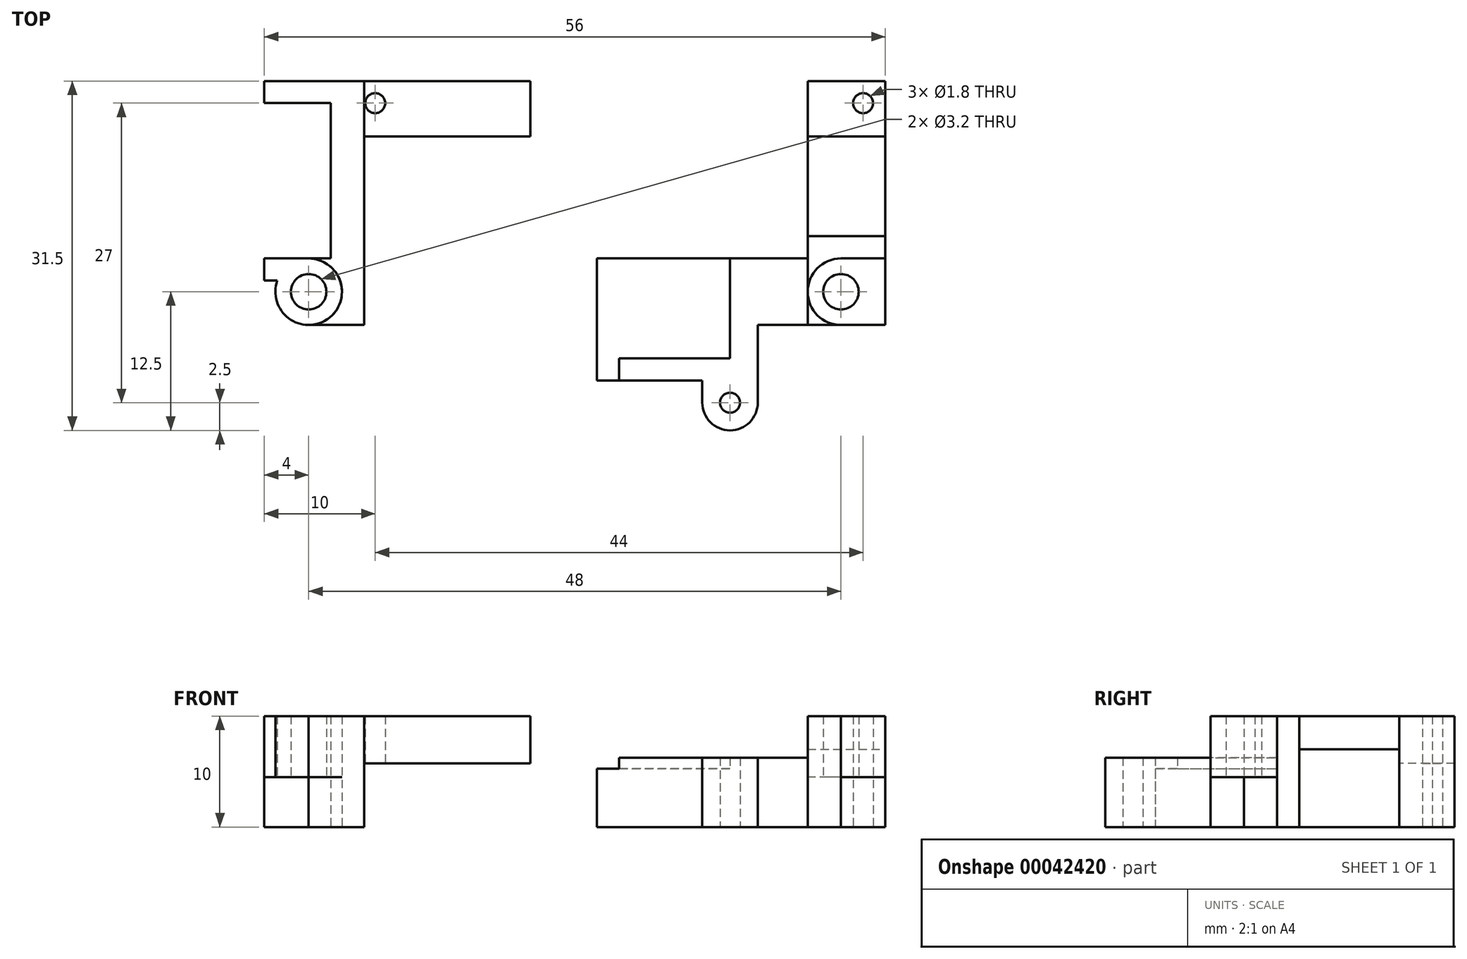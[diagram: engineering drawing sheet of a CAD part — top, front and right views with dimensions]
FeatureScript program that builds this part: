
annotation { "Feature Type Name" : "Feature", "Feature Type Description" : "" }
export const myFeature = defineFeature(function(context is Context, id is Id, definition is map)
    precondition{}
    {
        {
            var Q0;
            Q0=qCreatedBy(makeId("Top.planeOp"),FACE);
            var sketch = newSketch(context, id + "F0", { "sketchPlane" : qUnion([Q0])});
            skCircle(sketch, "E0", {"center": v(-24, 0) * mm, "radius": 1.6 * mm});
            skCircle(sketch, "E1", {"center": v(24, 0) * mm, "radius": 1.6 * mm});
            skCircle(sketch, "E2", {"center": v(26, 17) * mm, "radius": 0.9 * mm});
            skCircle(sketch, "E3", {"center": v(-24, 0) * mm, "radius": 3 * mm});
            skCircle(sketch, "E4", {"center": v(24, 0) * mm, "radius": 3 * mm});
            skLineSegment(sketch, "E5", {"start": v(-19, 19) * mm, "end": v(-19, -3) * mm});
            skLineSegment(sketch, "E6", {"start": v(-19, -3) * mm, "end": v(-24, -3) * mm});
            skLineSegment(sketch, "E7", {"start": v(2, 32) * mm, "end": v(2, -35.95) * mm, "construction": true});
            skLineSegment(sketch, "E8", {"start": v(2, -8) * mm, "end": v(-19, -8) * mm, "construction": true});
            skLineSegment(sketch, "E9", {"start": v(-19, -3) * mm, "end": v(-19, -8) * mm, "construction": true});
            skLineSegment(sketch, "E10", {"start": v(28, 3) * mm, "end": v(2, 3) * mm});
            skLineSegment(sketch, "E11", {"start": v(28, -3) * mm, "end": v(14, -3) * mm});
            skLineSegment(sketch, "E12", {"start": v(2, -3) * mm, "end": v(2, 3) * mm});
            skLineSegment(sketch, "E13", {"start": v(26, 17) * mm, "end": v(-28.96, 17) * mm, "construction": true});
            skLineSegment(sketch, "E14", {"start": v(-28, 33.68) * mm, "end": v(-28, -20.87) * mm, "construction": true});
            skLineSegment(sketch, "E15", {"start": v(-19, 3) * mm, "end": v(-28, 3) * mm});
            skLineSegment(sketch, "E16", {"start": v(-28, 3) * mm, "end": v(-28, 1) * mm});
            skLineSegment(sketch, "E17", {"start": v(-19, 19) * mm, "end": v(-22, 19) * mm});
            skLineSegment(sketch, "E18", {"start": v(-22, 19) * mm, "end": v(-22, 3) * mm});
            skLineSegment(sketch, "E19", {"start": v(-22, 19) * mm, "end": v(-28, 19) * mm});
            skLineSegment(sketch, "E20", {"start": v(-28, 19) * mm, "end": v(-28, 17) * mm});
            skLineSegment(sketch, "E21", {"start": v(-28, 17) * mm, "end": v(-22, 17) * mm});
            skLineSegment(sketch, "E22", {"start": v(21, 0) * mm, "end": v(21, -3) * mm});
            skCircle(sketch, "E23", {"center": v(14, -10) * mm, "radius": 0.9 * mm});
            skCircle(sketch, "E24", {"center": v(14, -10) * mm, "radius": 2.5 * mm});
            skLineSegment(sketch, "E25", {"start": v(16.5, -3) * mm, "end": v(16.5, -10) * mm});
            skLineSegment(sketch, "E26", {"start": v(2, -3) * mm, "end": v(2, -8) * mm});
            skLineSegment(sketch, "E27", {"start": v(-21, 3) * mm, "end": v(-21, 0) * mm});
            skLineSegment(sketch, "E28", {"start": v(-21, -3) * mm, "end": v(-21, 0) * mm});
            skLineSegment(sketch, "E29", {"start": v(-19, 19) * mm, "end": v(-4, 19) * mm});
            skLineSegment(sketch, "E30", {"start": v(-4, 19) * mm, "end": v(-4, 14) * mm});
            skLineSegment(sketch, "E31", {"start": v(-4, 14) * mm, "end": v(-19, 14) * mm});
            skLineSegment(sketch, "E32", {"start": v(28, -3) * mm, "end": v(28, 3) * mm});
            skLineSegment(sketch, "E33", {"start": v(28, 3) * mm, "end": v(28, 19) * mm});
            skLineSegment(sketch, "E34", {"start": v(28, 19) * mm, "end": v(21, 19) * mm});
            skLineSegment(sketch, "E35", {"start": v(21, 19) * mm, "end": v(21, 0) * mm});
            skCircle(sketch, "E36", {"center": v(26, 17) * mm, "radius": 1.5 * mm});
            skLineSegment(sketch, "E37", {"start": v(21, 14) * mm, "end": v(28, 14) * mm});
            skLineSegment(sketch, "E38", {"start": v(21, 5) * mm, "end": v(28, 5) * mm});
            skCircle(sketch, "E39", {"center": v(-18, 17) * mm, "radius": 0.9 * mm});
            skLineSegment(sketch, "E40", {"start": v(14, -6) * mm, "end": v(14, 3) * mm});
            skLineSegment(sketch, "E41", {"start": v(4, -6) * mm, "end": v(14, -6) * mm});
            skLineSegment(sketch, "E42", {"start": v(11.5, -8) * mm, "end": v(11.5, -10) * mm});
            skLineSegment(sketch, "E43", {"start": v(2, -8) * mm, "end": v(11.5, -8) * mm});
            skLineSegment(sketch, "E44", {"start": v(4, -6) * mm, "end": v(4, -8) * mm});
            skLineSegment(sketch, "E45", {"start": v(-28, 1) * mm, "end": v(-26.83, 1) * mm});
            skSolve(sketch);
        }
        {
            var Q0;
            {var subQ1=sQuery(id+"F0.wireOp",EDGE,"E29");Q0=makeQuery(id+"F0.imprint","IMPRINT",FACE,{"disambiguationData":[TD([[makeQuery(id+"F0.imprint","IMPRINT",EDGE,{"derivedFrom":subQ1}),-1.0]])]});}
            extrude(context, id + "F1", {"entities" : qUnion([Q0]), "depth" : 10 * mm, "hasSecondDirection" : true, "secondDirectionOppositeDirection" : false, "secondDirectionDepth" : 5.75 * mm});
        }
        {
            var Q0;
            {var subQ4=sQuery(id+"F0.wireOp",EDGE,"E25");Q0=makeQuery(id+"F0.imprint","IMPRINT",FACE,{"disambiguationData":[TD([[makeQuery(id+"F0.imprint","IMPRINT",EDGE,{"derivedFrom":subQ4}),-1.0]])]});}
            var Q1;
            Q1=makeQuery(id+"F0.imprint","IMPRINT",FACE,{"disambiguationData":[TD([[makeQuery(id+"F0.imprint","IMPRINT",EDGE,{"derivedFrom":sQuery(id+"F0.wireOp",EDGE,"E23")}),-1.0]])]});
            var Q2;
            {var subQ5=sQuery(id+"F0.wireOp",EDGE,"E22");Q2=makeQuery(id+"F0.imprint","IMPRINT",FACE,{"disambiguationData":[TD([[makeQuery(id+"F0.imprint","IMPRINT",EDGE,{"derivedFrom":subQ5}),-1.0]])]});}
            extrude(context, id + "F2", {"entities" : qUnion([Q0, Q1, Q2]), "depth" : 6.25 * mm});
        }
        {
            var Q0;
            {var subQ1=sQuery(id+"F0.wireOp",EDGE,"E37");Q0=makeQuery(id+"F0.imprint","IMPRINT",FACE,{"disambiguationData":[TD([[makeQuery(id+"F0.imprint","IMPRINT",EDGE,{"derivedFrom":subQ1}),-1.0]])]});}
            extrude(context, id + "F3", {"entities" : qUnion([Q0]), "depth" : 7 * mm});
        }
        {
            var Q0;
            {var subQ8=sQuery(id+"F0.wireOp",EDGE,"E12");Q0=makeQuery(id+"F0.imprint","IMPRINT",FACE,{"disambiguationData":[TD([[makeQuery(id+"F0.imprint","IMPRINT",EDGE,{"derivedFrom":subQ8}),-1.0]])]});}
            extrude(context, id + "F4", {"entities" : qUnion([Q0]), "operationType" : NewBodyOperationType.ADD, "depth" : 5.25 * mm});
        }
        {
            var Q0;
            {var subQ1=sQuery(id+"F0.wireOp",EDGE,"E19");Q0=makeQuery(id+"F0.imprint","IMPRINT",FACE,{"disambiguationData":[TD([[makeQuery(id+"F0.imprint","IMPRINT",EDGE,{"derivedFrom":subQ1}),1.0]])]});}
            var Q1;
            {var subQ0=sQuery(id+"F0.wireOp",EDGE,"E17");Q1=makeQuery(id+"F0.imprint","IMPRINT",FACE,{"disambiguationData":[TD([[makeQuery(id+"F0.imprint","IMPRINT",EDGE,{"derivedFrom":subQ0}),1.0]])]});}
            var Q2;
            {var subQ6=sQuery(id+"F0.wireOp",EDGE,"E27");Q2=makeQuery(id+"F0.imprint","IMPRINT",FACE,{"disambiguationData":[TD([[makeQuery(id+"F0.imprint","IMPRINT",EDGE,{"derivedFrom":subQ6}),1.0]])]});}
            var Q3;
            {var subQ0=sQuery(id+"F0.wireOp",EDGE,"E27");Q3=makeQuery(id+"F0.imprint","IMPRINT",FACE,{"disambiguationData":[TD([[makeQuery(id+"F0.imprint","IMPRINT",EDGE,{"derivedFrom":subQ0}),-1.0]])]});}
            var Q4;
            {var subQ0=sQuery(id+"F0.wireOp",EDGE,"E28");Q4=makeQuery(id+"F0.imprint","IMPRINT",FACE,{"disambiguationData":[TD([[makeQuery(id+"F0.imprint","IMPRINT",EDGE,{"derivedFrom":subQ0}),1.0]])]});}
            var Q5;
            {var subQ2=sQuery(id+"F0.wireOp",EDGE,"E34");Q5=makeQuery(id+"F0.imprint","IMPRINT",FACE,{"disambiguationData":[TD([[makeQuery(id+"F0.imprint","IMPRINT",EDGE,{"derivedFrom":subQ2}),1.0]])]});}
            var Q6;
            Q6=makeQuery(id+"F0.imprint","IMPRINT",FACE,{"disambiguationData":[TD([[makeQuery(id+"F0.imprint","IMPRINT",EDGE,{"derivedFrom":sQuery(id+"F0.wireOp",EDGE,"E2")}),-1.0]])]});
            var Q7;
            {var subQ0=sQuery(id+"F0.wireOp",EDGE,"E38");Q7=makeQuery(id+"F0.imprint","IMPRINT",FACE,{"disambiguationData":[TD([[makeQuery(id+"F0.imprint","IMPRINT",EDGE,{"derivedFrom":subQ0}),-1.0]])]});}
            var Q8;
            {var subQ0=sQuery(id+"F0.wireOp",EDGE,"E35");var subQ1=sQuery(id+"F0.wireOp",EDGE,"E10");var subQ2=makeQuery(id+"F0.imprint","INTERSECT",VERTEX,{"derivedFrom":[subQ1,subQ0]});Q8=makeQuery(id+"F0.imprint","IMPRINT",FACE,{"disambiguationData":[TD([[makeQuery(id+"F0.imprint","IMPRINT",EDGE,{"disambiguationData":[TD([[subQ2,1.0]])],"derivedFrom":subQ1}),1.0]])]});}
            var Q9;
            {var subQ0=sQuery(id+"F0.wireOp",EDGE,"E22");Q9=makeQuery(id+"F0.imprint","IMPRINT",FACE,{"disambiguationData":[TD([[makeQuery(id+"F0.imprint","IMPRINT",EDGE,{"derivedFrom":subQ0}),1.0]])]});}
            extrude(context, id + "F5", {"entities" : qUnion([Q0, Q1, Q2, Q3, Q4, Q5, Q6, Q7, Q8, Q9]), "depth" : 10 * mm});
        }
        {
            var Q0;
            Q0=makeQuery(id+"F0.imprint","IMPRINT",FACE,{"disambiguationData":[TD([[makeQuery(id+"F0.imprint","IMPRINT",EDGE,{"derivedFrom":sQuery(id+"F0.wireOp",EDGE,"E0")}),-1.0]])]});
            var Q1;
            {var subQ0=sQuery(id+"F0.wireOp",EDGE,"E16");Q1=makeQuery(id+"F0.imprint","IMPRINT",FACE,{"disambiguationData":[TD([[makeQuery(id+"F0.imprint","IMPRINT",EDGE,{"derivedFrom":subQ0}),1.0]])]});}
            var Q2;
            {var subQ0=sQuery(id+"F0.wireOp",EDGE,"E32");Q2=makeQuery(id+"F0.imprint","IMPRINT",FACE,{"disambiguationData":[TD([[makeQuery(id+"F0.imprint","IMPRINT",EDGE,{"derivedFrom":subQ0}),1.0]])]});}
            var Q3;
            Q3=makeQuery(id+"F0.imprint","IMPRINT",FACE,{"disambiguationData":[TD([[makeQuery(id+"F0.imprint","IMPRINT",EDGE,{"derivedFrom":sQuery(id+"F0.wireOp",EDGE,"E1")}),-1.0]])]});
            extrude(context, id + "F6", {"entities" : qUnion([Q0, Q1, Q2, Q3]), "depth" : 10 * mm, "hasSecondDirection" : true, "secondDirectionOppositeDirection" : false, "secondDirectionDepth" : 4.5 * mm});
        }
    });
